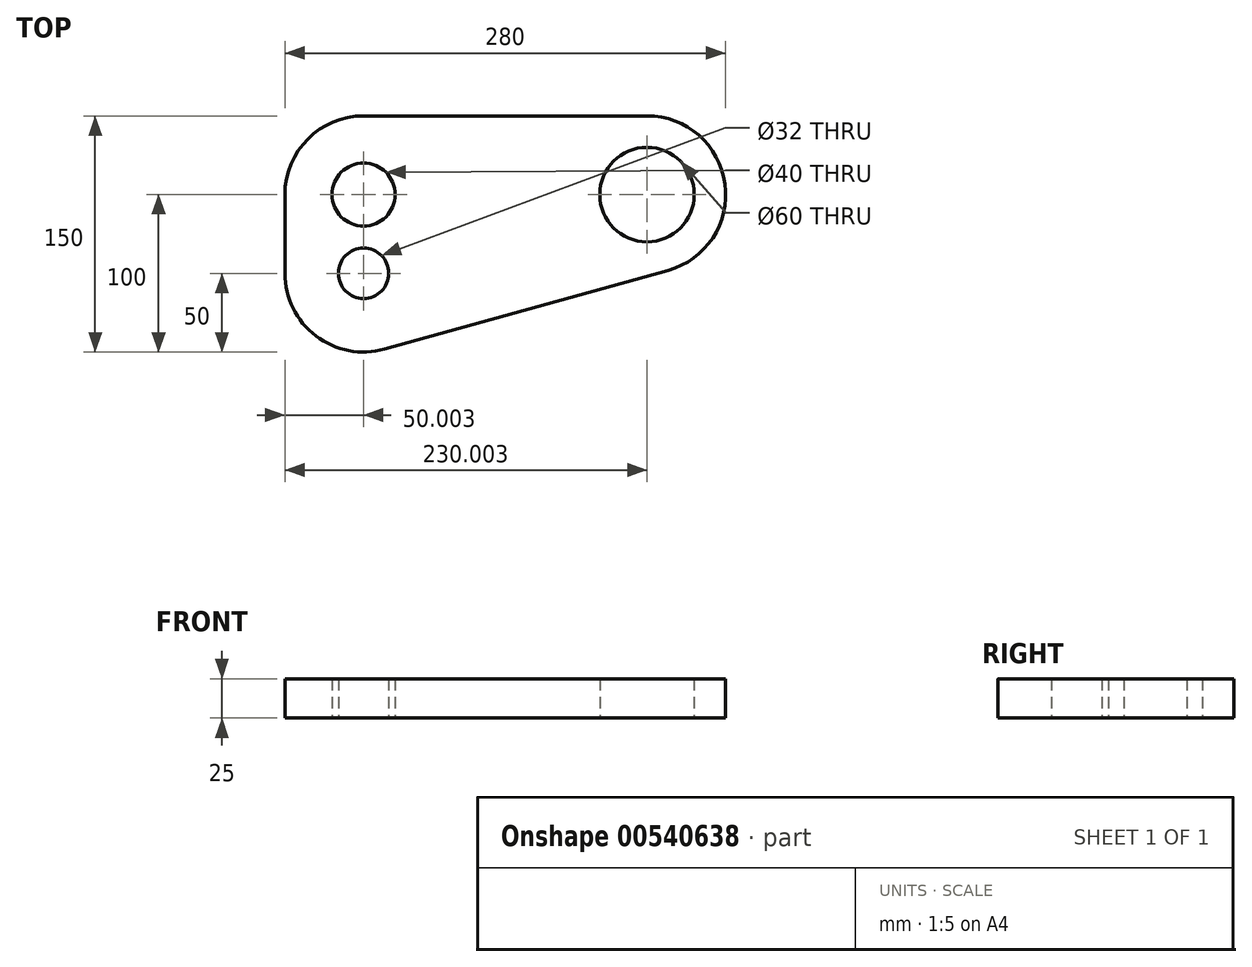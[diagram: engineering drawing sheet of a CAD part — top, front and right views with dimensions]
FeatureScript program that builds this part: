
annotation { "Feature Type Name" : "Feature", "Feature Type Description" : "" }
export const myFeature = defineFeature(function(context is Context, id is Id, definition is map)
    precondition{}
    {
        {
            var Q0;
            Q0=qCreatedBy(makeId("Top.planeOp"),FACE);
            var sketch = newSketch(context, id + "F0", { "sketchPlane" : qUnion([Q0])});
            skCircle(sketch, "E0", {"center": v(-89.47, -50) * mm, "radius": 20 * mm});
            skCircle(sketch, "E1", {"center": v(-89.47, -50) * mm, "radius": 10 * mm});
            skPoint(sketch, "E2.trimOffspring.end.orphan", {"position": v(-108.34, -47.25) * mm});
            skArc(sketch, "E3", {"start": v(-89.47, 0) * mm, "mid": v(-124.82, -14.64) * mm, "end": v(-139.47, -50) * mm});
            skPoint(sketch, "E4.center.orphan", {"position": v(-89.5, -47.25) * mm});
            skArc(sketch, "E5", {"start": v(-139.47, -100) * mm, "mid": v(-119.72, -139.8) * mm, "end": v(-76.09, -148.18) * mm});
            skCircle(sketch, "E6", {"center": v(-89.47, -100) * mm, "radius": 16 * mm});
            skLineSegment(sketch, "E7", {"start": v(-139.47, -50) * mm, "end": v(-139.47, -100) * mm});
            skLineSegment(sketch, "E8", {"start": v(-89.47, -50) * mm, "end": v(90.53, -50) * mm});
            skArc(sketch, "E9", {"start": v(103.91, -98.18) * mm, "mid": v(140.07, -43.25) * mm, "end": v(90.53, 0) * mm});
            skCircle(sketch, "E10", {"center": v(90.53, -50) * mm, "radius": 16 * mm});
            skCircle(sketch, "E11", {"center": v(90.53, -50) * mm, "radius": 30 * mm});
            skLineSegment(sketch, "E12", {"start": v(-89.47, 0) * mm, "end": v(90.53, 0) * mm});
            skLineSegment(sketch, "E13", {"start": v(-76.09, -148.18) * mm, "end": v(103.91, -98.18) * mm});
            skSolve(sketch);
        }
        {
            var Q0;
            Q0=makeQuery(id+"F0.imprint","IMPRINT",FACE,{"disambiguationData":[TD([[makeQuery(id+"F0.imprint","IMPRINT",EDGE,{"derivedFrom":sQuery(id+"F0.wireOp",EDGE,"E0")}),-1.0]])]});
            extrude(context, id + "F1", {"entities" : qUnion([Q0]), "depth" : 25 * mm, "offsetDistance" : 25 * mm});
        }
    });
